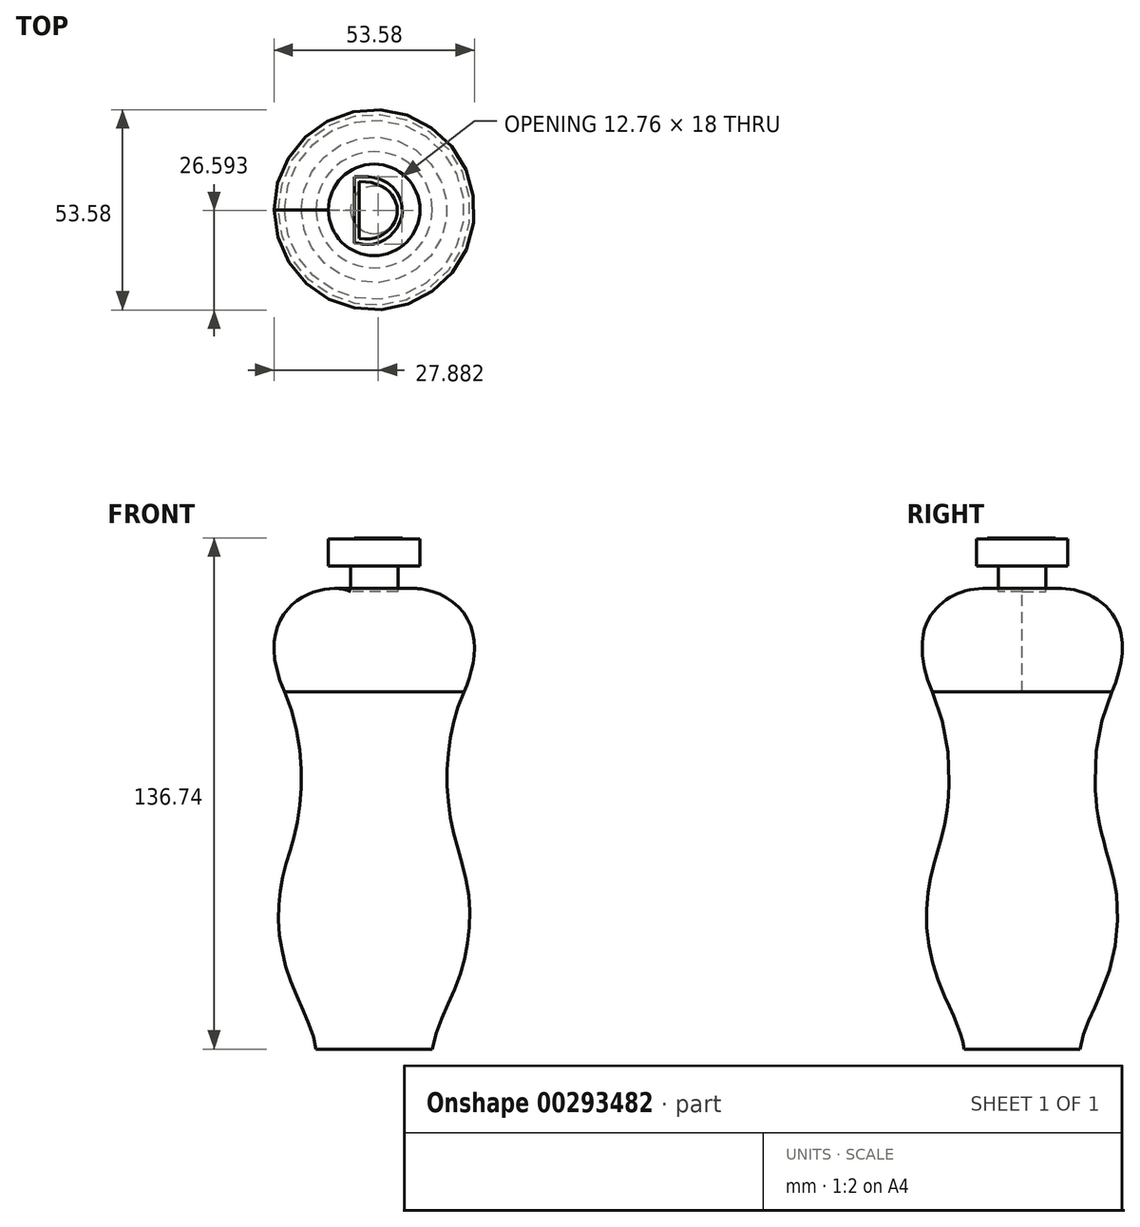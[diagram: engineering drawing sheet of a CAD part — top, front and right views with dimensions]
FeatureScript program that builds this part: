
annotation { "Feature Type Name" : "Feature", "Feature Type Description" : "" }
export const myFeature = defineFeature(function(context is Context, id is Id, definition is map)
    precondition{}
    {
        {
            var Q0;
            Q0=qCreatedBy(makeId("Front.planeOp"),FACE);
            var sketch = newSketch(context, id + "F0", { "sketchPlane" : qUnion([Q0])});
            skFitSpline(sketch, "E0", {"points": [v(-31.06, 58.36) * mm, v(-24, 34.12) * mm, v(-20.47, 0) * mm, v(-25.18, -19.3) * mm, v(-22.83, -41.89) * mm, v(-15.53, -61.42) * mm], "startDerivative": vector(-75.98, -89.35) * mm, "endDerivative": vector(10.56, -91.61) * mm});
            skLineSegment(sketch, "E1", {"start": v(-15.53, -61.42) * mm, "end": v(0, -61.42) * mm});
            skLineSegment(sketch, "E2", {"start": v(-6.35, 60.95) * mm, "end": v(-6.35, 67.77) * mm});
            skLineSegment(sketch, "E3", {"start": v(-6.35, 67.77) * mm, "end": v(-12.24, 67.77) * mm});
            skLineSegment(sketch, "E4", {"start": v(-12.24, 67.77) * mm, "end": v(-12.24, 75.07) * mm});
            skLineSegment(sketch, "E5", {"start": v(-12.24, 75.07) * mm, "end": v(0, 75.07) * mm});
            skLineSegment(sketch, "E6", {"start": v(0, 75.07) * mm, "end": v(0, -61.42) * mm});
            skFitSpline(sketch, "E7", {"points": [v(-24, 34.12) * mm, v(-6.35, 60.95) * mm], "startDerivative": vector(-31.77, 74.13) * mm, "endDerivative": vector(16.94, -9.88) * mm});
            skPoint(sketch, "E8.endDerivative.orphan", {"position": v(-12.24, 60.1) * mm});
            skSolve(sketch);
        }
        {
            var Q0;
            Q0=makeQuery(id+"F0.imprint","IMPRINT",FACE,{"disambiguationData":[TD([[makeQuery(id+"F0.imprint","IMPRINT",EDGE,{"derivedFrom":sQuery(id+"F0.wireOp",EDGE,"E0")}),1.0]])]});
            var Q1;
            Q1=sQuery(id+"F0.wireOp",EDGE,"E6");
            revolve(context, id + "F1", {"entities" : qUnion([Q0]), "axis" : qUnion([Q1]), "revolveType" : RevolveType.FULL});
        }
        {
            var Q0;
            Q0=makeQuery(id+"F1.opRevolve","SWEPT_FACE",FACE,{"disambiguationData":[OSD([sQuery(id+"F0.wireOp",EDGE,"E5")])]});
            var sketch = newSketch(context, id + "F2", { "sketchPlane" : qUnion([Q0])});
            skLineSegment(sketch, "E9", {"start": v(-4.02, 7.54) * mm, "end": v(-4.02, -7.71) * mm});
            skFitSpline(sketch, "E10", {"points": [v(-4.02, 7.54) * mm, v(6.15, -0.9) * mm, v(-4.02, -7.71) * mm], "startDerivative": vector(41.6, 1.46) * mm, "endDerivative": vector(-34.87, 5.3) * mm});
            skFitSpline(sketch, "E11.0", {"points": [v(-4.06, 8.8) * mm, v(-2.2, 8.87) * mm, v(1.16, 8.39) * mm, v(4.88, 6.17) * mm, v(6.74, 3.48) * mm, v(7.41, 1.1) * mm, v(7.5, -0.75) * mm, v(7.17, -2.56) * mm, v(6.45, -4.26) * mm, v(5.37, -5.8) * mm, v(3.5, -7.55) * mm, v(0.44, -9.05) * mm, v(-2.6, -9.21) * mm, v(-4.2, -8.97) * mm]});
            skLineSegment(sketch, "E12.0", {"start": v(-5.29, 7.54) * mm, "end": v(-5.29, -7.71) * mm});
            skLineSegment(sketch, "E13", {"start": v(-5.29, 7.54) * mm, "end": v(-5.29, 8.8) * mm});
            skLineSegment(sketch, "E14", {"start": v(-5.29, 8.8) * mm, "end": v(-4.06, 8.8) * mm});
            skLineSegment(sketch, "E15", {"start": v(-5.29, -7.71) * mm, "end": v(-5.29, -8.97) * mm});
            skLineSegment(sketch, "E16", {"start": v(-5.29, -8.97) * mm, "end": v(-4.2, -8.97) * mm});
            skSolve(sketch);
        }
        {
            var Q0;
            Q0 = qSketchRegion(id + "F2", true);
            extrude(context, id + "F3", {"entities" : qUnion([Q0]), "depth" : 0.25 * mm});
        }
    });
